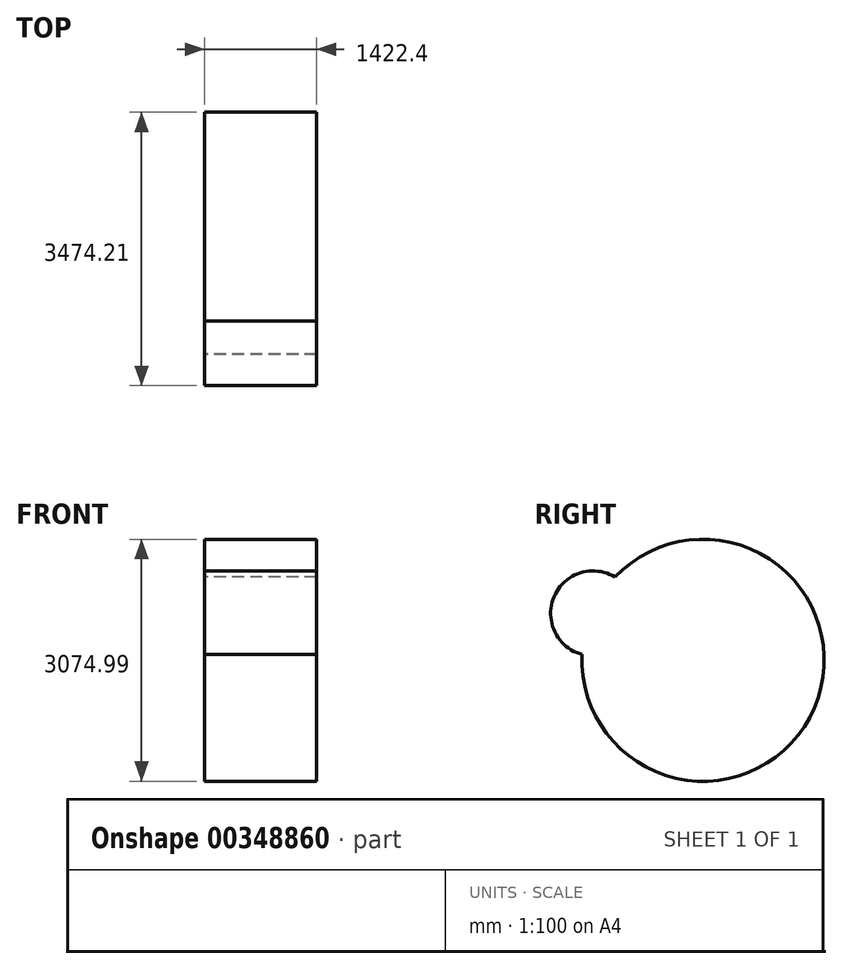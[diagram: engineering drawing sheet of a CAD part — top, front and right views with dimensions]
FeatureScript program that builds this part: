
annotation { "Feature Type Name" : "Feature", "Feature Type Description" : "" }
export const myFeature = defineFeature(function(context is Context, id is Id, definition is map)
    precondition{}
    {
        {
            var Q0;
            Q0=qCreatedBy(makeId("Right.planeOp"),FACE);
            var sketch = newSketch(context, id + "F0", { "sketchPlane" : qUnion([Q0])});
            skLineSegment(sketch, "E0", {"start": v(-669.82, 601.35) * mm, "end": v(211.68, 0) * mm});
            skArc(sketch, "E1", {"start": v(211.68, 0) * mm, "mid": v(72.76, 1061.6) * mm, "end": v(-66.15, 0) * mm});
            skArc(sketch, "E2", {"start": v(-66.15, 0) * mm, "mid": v(2924.07, -571.63) * mm, "end": v(211.68, 810.8) * mm});
            skArc(sketch, "E3", {"start": v(4167.36, -3196.88) * mm, "mid": v(3241.8, -2210.7) * mm, "end": v(2109.3, -1471.34) * mm});
            skSolve(sketch);
        }
        {
            var Q0;
            Q0 = qSketchRegion(id + "F0", true);
            extrude(context, id + "F1", {"entities" : qUnion([Q0]), "depth" : 1422.4 * mm});
        }
    });
